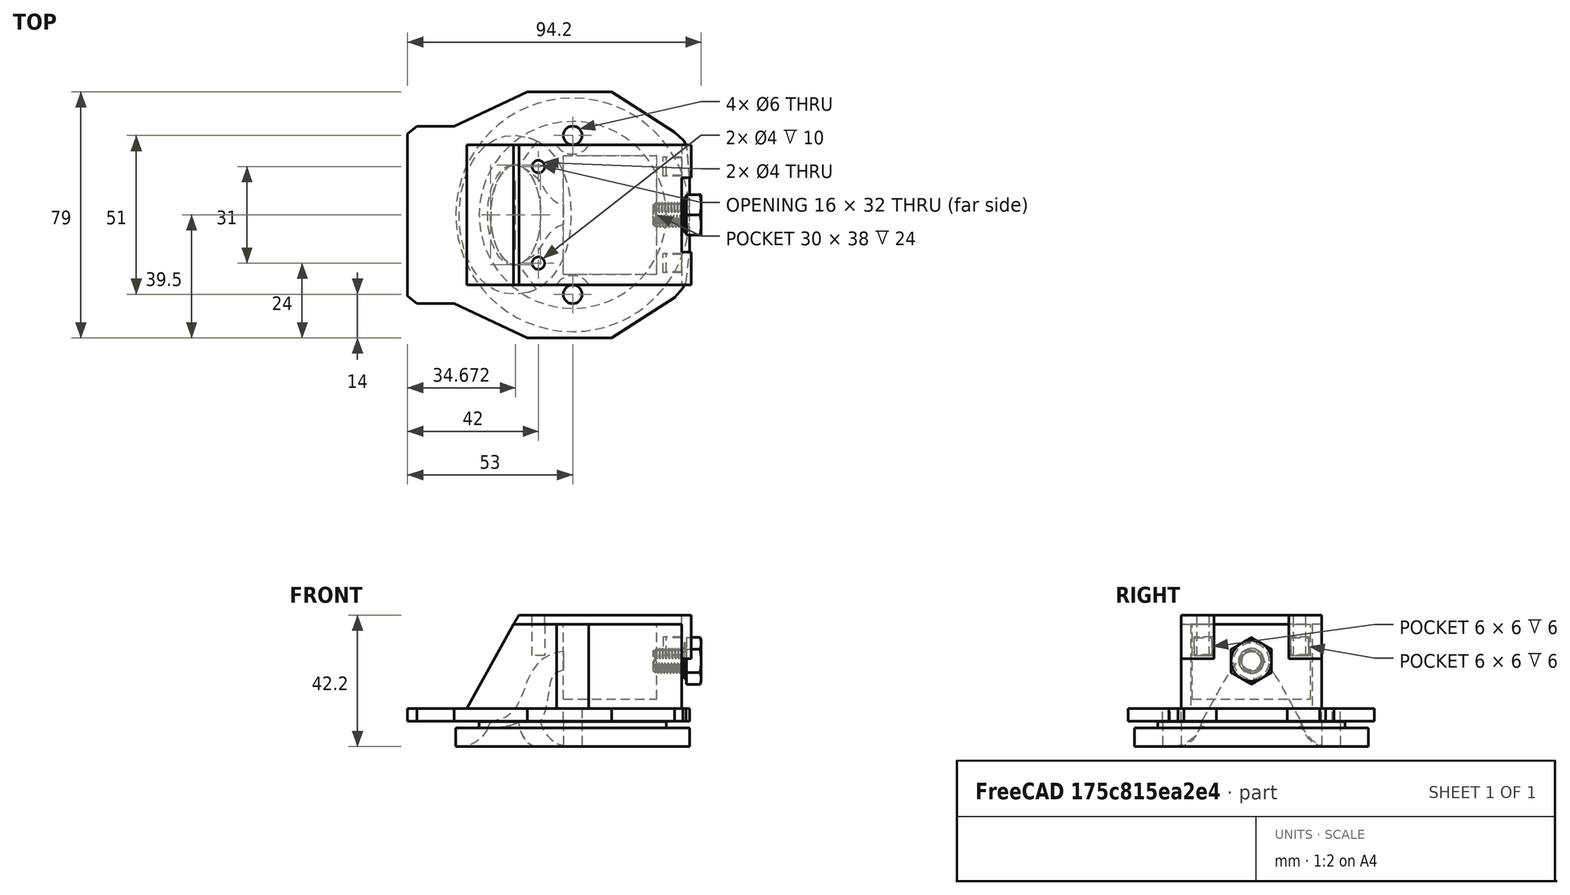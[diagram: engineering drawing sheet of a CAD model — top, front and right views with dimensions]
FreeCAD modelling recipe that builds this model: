
FCSTD DOCUMENT  (FreeCAD 1.0R39109 (Git))
Label: cup spool
License: All rights reserved
LicenseURL: https://en.wikipedia.org/wiki/All_rights_reserved
objects: Sketcher::SketchObject×17, PartDesign::Pad×6, Mesh::Feature×5, PartDesign::Pocket×4, PartDesign::Body×3, PartDesign::SubtractiveBox×1, Part::FeaturePython×1, PartDesign::SubtractivePipe×1, App::Part×1, PartDesign::AdditiveLoft×1, PartDesign::SubtractiveLoft×1, PartDesign::Fillet×1
note: 83 computed .brp shape members not serialized (recipe doc carries the construction recipe); baked Part::Feature solids carry a one-line shape summary decoded from their .brp

FEATURE [Mesh::Feature] cup_spool_bolt  label="bolt"
  Placement = pos=(23.83,0,17.89) rot=(0,1,0;0.785398rad)
FEATURE [Mesh::Feature] cup_spool_bottom_cylinder  label="cup spool bottom cylinder"
FEATURE [Mesh::Feature] cup_spool_cup_cylinder  label="cup spool cup cylinder"
FEATURE [Mesh::Feature] cup_spool_cup  label="cup spool cup"
  Placement = pos=(-0.2,1.9,-4) rot=(0,0,1;0rad)
FEATURE [Sketcher::SketchObject] Sketch
  ArcFitTolerance = 1e-06
  AttachmentSupport = -> [XY_Plane]
  FullyConstrained = true
  MakeInternals = false
  MapMode = 5
  sketch-geometry (1):
    g0: Circle CenterX=0 CenterY=0 CenterZ=0 NormalX=0 NormalY=0 NormalZ=1 AngleXU=0 Radius=37.5
  constraints (2):
    c: Coincident(g0,g-1)
    c: Diameter(g0) = 75
FEATURE [PartDesign::Pad] Pad
  Direction = (0,0,1)
  Length = 6
  Length2 = 10
  Profile = -> Sketch
  ReferenceAxis = -> Sketch [N_Axis]
  Refine = true
  Suppressed = false
  Type = 0
FEATURE [Sketcher::SketchObject] Sketch001
  ArcFitTolerance = 1e-06
  AttachmentSupport = -> [Pad]
  FullyConstrained = true
  MakeInternals = false
  MapMode = 5
  Placement = pos=(0,0,6) rot=(0,0,1;0rad)
  sketch-geometry (1):
    g0: Circle CenterX=0 CenterY=0 CenterZ=0 NormalX=0 NormalY=0 NormalZ=1 AngleXU=0 Radius=30
  constraints (2):
    c: Coincident(g0,g-1)
    c: Diameter(g0) = 60
FEATURE [PartDesign::Pad] Pad001
  BaseFeature = -> Pad
  Direction = (0,0,1)
  Length = 2
  Length2 = 10
  Profile = -> Sketch001
  ReferenceAxis = -> Sketch001 [N_Axis]
  Refine = true
  Suppressed = false
  Type = 0
FEATURE [Sketcher::SketchObject] Sketch002
  ArcFitTolerance = 1e-06
  AttachmentSupport = -> [XY_Plane001]
  FullyConstrained = true
  MakeInternals = false
  MapMode = 5
  sketch-geometry (18):
    g0: LineSegment StartX=-53 StartY=26 StartZ=0 EndX=-53 EndY=-26 EndZ=0
    g1: LineSegment StartX=-53 StartY=-26 StartZ=0 EndX=-50 EndY=-28.5 EndZ=0
    g2: LineSegment StartX=-50 StartY=-28.5 StartZ=0 EndX=-38 EndY=-28.5 EndZ=0
    g3: LineSegment StartX=-38 StartY=-28.5 StartZ=0 EndX=-14.5 EndY=-39.5 EndZ=0
    g4: LineSegment StartX=-14.5 StartY=-39.5 StartZ=0 EndX=12.5 EndY=-39.5 EndZ=0
    g5: LineSegment StartX=12.5 StartY=-39.5 StartZ=0 EndX=32.6742 EndY=-26.5 EndZ=0
    g6: LineSegment StartX=36.4381 StartY=-21.6053 StartZ=0 EndX=37.5 EndY=-11.2321 EndZ=0
    g7: LineSegment StartX=37.5 StartY=-11.2321 StartZ=0 EndX=37.5 EndY=11.5 EndZ=0
    g8: LineSegment StartX=37.5 StartY=11.5 StartZ=0 EndX=36.6742 EndY=21.8947 EndZ=0
    g9: LineSegment StartX=32.6742 StartY=26.5 StartZ=0 EndX=12.5 EndY=39.5 EndZ=0
    g10: LineSegment StartX=12.5 StartY=39.5 StartZ=0 EndX=-14.5 EndY=39.5 EndZ=0
    g11: LineSegment StartX=-14.5 StartY=39.5 StartZ=0 EndX=-38 EndY=28.5 EndZ=0
    g12: LineSegment StartX=-38 StartY=28.5 StartZ=0 EndX=-50 EndY=28.5 EndZ=0
    g13: LineSegment StartX=-50 StartY=28.5 StartZ=0 EndX=-53 EndY=26 EndZ=0
    g14: LineSegment StartX=32.6742 StartY=26.5 StartZ=0 EndX=35.6742 EndY=23.8542 EndZ=0
    g15: LineSegment StartX=35.6742 StartY=23.8542 StartZ=0 EndX=36.6742 EndY=21.8947 EndZ=0
    g16: LineSegment StartX=32.6742 StartY=-26.5 StartZ=0 EndX=35.32 EndY=-23.5 EndZ=0
    g17: LineSegment StartX=35.32 StartY=-23.5 StartZ=0 EndX=36.4381 EndY=-21.6053 EndZ=0
  constraints (54):
    c: Vertical(g0)
    c: Horizontal(g4)
    c: Vertical(g7)
    c: Horizontal(g10)
    c: DistanceY(g0,g0) = 52
    c: Distance(g0,g-1) = 26
    c: Distance(g-1,g0) = 53
    c: Coincident(g13,g0)
    c: Coincident(g1,g0)
    c: DistanceX(g0,g13) = 3
    c: DistanceY(g0,g13) = 2.5
    c: DistanceY(g1,g0) = 2.5
    c: DistanceX(g0,g1) = 3
    c: Parallel(g2,g-1)
    c: Parallel(g12,g-1)
    c: Coincident(g12,g13)
    c: DistanceX(g12,g12) = 12
    c: Coincident(g1,g2)
    c: Equal(g2,g12)
    c: Coincident(g2,g3)
    c: Coincident(g12,g11)
    c: Equal(g11,g3)
    c: Distance(g11,g-1) = 39.5
    c: Distance(g3,g-1) = 39.5
    c: DistanceX(g3,g-1) = 14.5
    c: Coincident(g10,g11)
    c: Coincident(g4,g3)
    c: Equal(g10,g4)
    c: DistanceX(g10,g10) = 27
    c: Coincident(g10,g9)
    c: Coincident(g4,g5)
    c: Equal(g5,g9)
    c: Distance(g5,g5) = 24
    c: DistanceY(g5,g-1) = 26.5
    c: Distance(g9,g-1) = 26.5
    c: Equal(g8,g6)
    c: Distance(g8,g-1) = 11.5
    c: Coincident(g6,g7)
    c: Coincident(g8,g7)
    c: Coincident(g5,g16)
    c: Coincident(g14,g9)
    c: Equal(g16,g14)
    c: DistanceX(g9,g14) = 3
    c: DistanceY(g5,g16) = 3
    c: Coincident(g16,g17)
    c: Coincident(g15,g14)
    c: Equal(g17,g15)
    c: Coincident(g17,g6)
    c: Coincident(g15,g8)
    c: Distance(g17,g17) = 2.2
    c: Distance(g16,g16) = 4
    c: DistanceY(g6,g8) = 43.5
    c: DistanceX(g14,g8) = 1
    c: Distance(g-2,g7) = 37.5
FEATURE [Mesh::Feature] cup_spool_cup001  label="cup spool cup001"
  Placement = pos=(-0.694658,0.312171,0) rot=(0,0,-1;0.017453rad)
FEATURE [PartDesign::Pad] Pad002
  Direction = (0,0,1)
  Length = 4
  Length2 = 10
  Profile = -> Sketch002
  ReferenceAxis = -> Sketch002 [N_Axis]
  Refine = true
  Suppressed = false
  Type = 0
FEATURE [Sketcher::SketchObject] Sketch003
  ArcFitTolerance = 1e-06
  AttachmentSupport = -> [XZ_Plane001]
  FullyConstrained = true
  MakeInternals = false
  MapMode = 5
  Placement = pos=(0,0,0) rot=(1,0,0;1.5708rad)
  sketch-geometry (4):
    g0: LineSegment StartX=35 StartY=31 StartZ=0 EndX=35 EndY=4 EndZ=0
    g1: LineSegment StartX=35 StartY=31 StartZ=0 EndX=-19 EndY=31 EndZ=0
    g2: LineSegment StartX=-19 StartY=31 StartZ=0 EndX=-34 EndY=4 EndZ=0
    g3: LineSegment StartX=35 StartY=4 StartZ=0 EndX=-34 EndY=4 EndZ=0
  constraints (12):
    c: Vertical(g0)
    c: Horizontal(g1)
    c: Horizontal(g3)
    c: DistanceY(g-1,g0) = 4
    c: Distance(g0,g-2) = 35
    c: DistanceY(g0,g0) = 27
    c: Coincident(g0,g3)
    c: DistanceX(g3,g3) = 69
    c: Coincident(g2,g3)
    c: Coincident(g1,g0)
    c: DistanceX(g1,g1) = 54
    c: Coincident(g2,g1)
FEATURE [PartDesign::Pad] Pad003
  BaseFeature = -> Pad002
  Direction = (0,-1,2e-16)
  Length = 45
  Length2 = 10
  Midplane = true
  Profile = -> Sketch003
  ReferenceAxis = -> Sketch003 [N_Axis]
  Refine = true
  Suppressed = false
  Type = 0
FEATURE [PartDesign::SubtractiveBox] Box
  AttacherType = Attacher::AttachEngine3D
  AttachmentOffset = pos=(-3,-19,7) rot=(0,0,1;0rad)
  AttachmentSupport = -> [XY_Plane001]
  BaseFeature = -> Pad003
  Height = 24
  Length = 30
  MapMode = 5
  Placement = pos=(-3,-19,7) rot=(0,0,1;0rad)
  Refine = true
  Suppressed = false
  Width = 38
FEATURE [Part::FeaturePython] Screw  label="M8x1x10-Screw"  # WARN: FeaturePython — macro-defined, semantics opaque (R4)
  Diameter = 1
  Invert = false
  LeftHanded = false
  Length = 8
  LengthCustom = 10
  MatchOuter = false
  OffsetAngle = 0
  Placement = pos=(35.9,0,19.3) rot=(0,1,0;1.5708rad)
  Thread = true
  Type = 91
FEATURE [Sketcher::SketchObject] Sketch004
  ArcFitTolerance = 1e-06
  AttachmentSupport = -> [Box]
  FullyConstrained = true
  MakeInternals = false
  MapMode = 5
  Placement = pos=(35,-19,7) rot=(0.57735,0.57735,0.57735;2.0944rad)
  sketch-geometry (8):
    g0: LineSegment StartX=0.5 StartY=20 StartZ=0 EndX=0.5 EndY=14 EndZ=0
    g1: LineSegment StartX=0.5 StartY=14 StartZ=0 EndX=6.5 EndY=14 EndZ=0
    g2: LineSegment StartX=6.5 StartY=14 StartZ=0 EndX=6.5 EndY=20 EndZ=0
    g3: LineSegment StartX=6.5 StartY=20 StartZ=0 EndX=0.5 EndY=20 EndZ=0
    g4: LineSegment StartX=31.5 StartY=20 StartZ=0 EndX=31.5 EndY=14 EndZ=0
    g5: LineSegment StartX=31.5 StartY=14 StartZ=0 EndX=37.5 EndY=14 EndZ=0
    g6: LineSegment StartX=37.5 StartY=14 StartZ=0 EndX=37.5 EndY=20 EndZ=0
    g7: LineSegment StartX=37.5 StartY=20 StartZ=0 EndX=31.5 EndY=20 EndZ=0
  constraints (24):
    c: Coincident(g0,g1)
    c: Coincident(g1,g2)
    c: Coincident(g2,g3)
    c: Coincident(g3,g0)
    c: Vertical(g0)
    c: Vertical(g2)
    c: Horizontal(g1)
    c: Horizontal(g3)
    c: Coincident(g4,g5)
    c: Coincident(g5,g6)
    c: Coincident(g6,g7)
    c: Coincident(g7,g4)
    c: Vertical(g4)
    c: Vertical(g6)
    c: Horizontal(g5)
    c: Horizontal(g7)
    c: DistanceX(g3,g3) = 6
    c: Equal(g3,g7)
    c: Equal(g2,g3)
    c: Equal(g4,g7)
    c: Distance(g-2,g0) = 0.5
    c: Distance(g-2,g6) = 37.5
    c: Distance(g-1,g1) = 14
    c: Distance(g-1,g5) = 14
FEATURE [PartDesign::Pocket] Pocket
  BaseFeature = -> Box
  Direction = (-1,0,0)
  Length = 6
  Length2 = 5
  Placement = pos=(-3,-19,7) rot=(0,0,1;0rad)
  Profile = -> Sketch004
  ReferenceAxis = -> Sketch004 [N_Axis]
  Refine = true
  Suppressed = false
  Type = 0
FEATURE [Sketcher::SketchObject] Sketch005
  ArcFitTolerance = 1e-06
  AttachmentSupport = -> [Pocket]
  FullyConstrained = true
  MakeInternals = false
  MapMode = 5
  Placement = pos=(-3,-19,31) rot=(0,0,1;0rad)
  sketch-geometry (2):
    g0: Circle CenterX=-8 CenterY=34.5 CenterZ=0 NormalX=0 NormalY=0 NormalZ=1 AngleXU=0 Radius=2
    g1: Circle CenterX=-8 CenterY=3.5 CenterZ=0 NormalX=0 NormalY=0 NormalZ=1 AngleXU=0 Radius=2
  constraints (6):
    c: Diameter(g0) = 4
    c: Diameter(g1) = 4
    c: Distance(g0,g-1) = 34.5
    c: Distance(g1,g-1) = 3.5
    c: Distance(g1,g-2) = 8
    c: Distance(g0,g-2) = 8
FEATURE [PartDesign::Pocket] Pocket001
  BaseFeature = -> Pocket
  Direction = (0,0,-1)
  Length = 10
  Length2 = 5
  Placement = pos=(-3,-19,7) rot=(0,0,1;0rad)
  Profile = -> Sketch005
  ReferenceAxis = -> Sketch005 [N_Axis]
  Refine = true
  Suppressed = false
  Type = 0
FEATURE [Sketcher::SketchObject] Sketch007  label="hole cleaner box"
  ArcFitTolerance = 1e-06
  AttachmentSupport = -> [Pocket001]
  FullyConstrained = false
  MakeInternals = false
  MapMode = 5
  Placement = pos=(-3,-19,7) rot=(0.57735,0.57735,0.57735;2.0944rad)
  sketch-geometry (1):
    g0: Circle CenterX=18.991 CenterY=12.3351 CenterZ=0 NormalX=0 NormalY=0 NormalZ=1 AngleXU=0 Radius=3
  constraints (1):
    c: Diameter(g0) = 6
FEATURE [Sketcher::SketchObject] Sketch008  label="hole bottom"
  ArcFitTolerance = 1e-06
  AttachmentSupport = -> [Pocket001]
  FullyConstrained = false
  MakeInternals = false
  MapMode = 5
  Placement = pos=(-3,-19,0) rot=(1,0,0;3.14159rad)
  sketch-geometry (5):
    g0: Ellipse CenterX=-15.3285 CenterY=-19 CenterZ=0 NormalX=0 NormalY=0 NormalZ=1 MajorRadius=16 MinorRadius=8 AngleXU=-1.5708
    g1: LineSegment [constr] StartX=-15.3285 StartY=-35 StartZ=0 EndX=-15.3285 EndY=-3 EndZ=0
    g2: LineSegment [constr] StartX=-7.32854 StartY=-19 StartZ=0 EndX=-23.3285 EndY=-19 EndZ=0
    g3: GeomPoint [constr] X=-15.3285 Y=-32.8564 Z=0
    g4: GeomPoint [constr] X=-15.3285 Y=-5.14359 Z=0
  constraints (5):
    c: InternalAlignment(g1-g4 -> g0) x4
    c: Distance(g0,g1) = 16
    c: Angle(g1) = 1.5708
    c: Distance(g0,g2) = 8
    c: Distance(g0,g-1) = 19
FEATURE [Sketcher::SketchObject] Sketch009  label="hole path"
  ArcFitTolerance = 1e-06
  AttachmentSupport = -> [XZ_Plane001]
  FullyConstrained = false
  MakeInternals = false
  MapMode = 5
  Placement = pos=(0,0,0) rot=(1,0,0;1.5708rad)
  sketch-geometry (7):
    g0-g3: Circle [constr] x4 (B-spline internal-alignment scaffolding for g4; pole/knot coordinates omitted)
    g4: BSplineCurve PolesCount=4 KnotsCount=2 Degree=3 IsPeriodic=0
    g5: GeomPoint [constr] X=-19.2845 Y=0 Z=0
    g6: GeomPoint [constr] X=-3.01587 Y=19.3204 Z=0
  constraints (8):
    c: Weight(g0) = 1
    c: Equal(g0,g1)
    c: Equal(g0,g2)
    c: Equal(g0,g3)
    c: InternalAlignment(g0-g3 -> g4) x4
    c: InternalAlignment(g5,g4)
    c: InternalAlignment(g6,g4)
    c: PointOnObject(g0,g-1)
FEATURE [PartDesign::SubtractivePipe] SubtractivePipe
  AuxilleryCurvelinear = true
  AuxillerySpineTangent = false
  BaseFeature = -> Pocket001
  Binormal = (0,0,0)
  Mode = 0
  Placement = pos=(-3,-19,7) rot=(0,0,1;0rad)
  Profile = -> Sketch007
  Refine = true
  Sections = -> [Sketch008]
  Spine = -> Sketch009
  SpineTangent = false
  Suppressed = false
  Transformation = 1
  Transition = 0
FEATURE [App::Part] Part  label="import"
  Group = -> [cup_spool_bottom_cylinder,cup_spool_cup_cylinder,cup_spool_cup,cup_spool_cup001]
  Origin = -> Origin003
FEATURE [Sketcher::SketchObject] Sketch010
  ArcFitTolerance = 1e-06
  AttachmentSupport = -> [XY_Plane002]
  FullyConstrained = true
  MakeInternals = false
  MapMode = 5
  sketch-geometry (6):
    g0: LineSegment StartX=-31 StartY=22.5 StartZ=0 EndX=-31 EndY=-22.5 EndZ=0
    g1: LineSegment StartX=-31 StartY=-22.5 StartZ=0 EndX=23 EndY=-22.5 EndZ=0
    g2: LineSegment StartX=23 StartY=-22.5 StartZ=0 EndX=23 EndY=22.5 EndZ=0
    g3: LineSegment StartX=23 StartY=22.5 StartZ=0 EndX=-31 EndY=22.5 EndZ=0
    g4: Circle CenterX=-23 CenterY=15.5 CenterZ=0 NormalX=0 NormalY=0 NormalZ=1 AngleXU=0 Radius=2
    g5: Circle CenterX=-23 CenterY=-15.5 CenterZ=0 NormalX=0 NormalY=0 NormalZ=1 AngleXU=0 Radius=2
  constraints (18):
    c: Coincident(g0,g1)
    c: Coincident(g1,g2)
    c: Coincident(g2,g3)
    c: Coincident(g3,g0)
    c: Vertical(g0)
    c: Vertical(g2)
    c: Horizontal(g1)
    c: Horizontal(g3)
    c: Distance(g-1,g1) = 22.5
    c: DistanceY(g0,g0) = 45
    c: DistanceX(g1,g1) = 54
    c: Diameter(g4) = 4
    c: Diameter(g5) = 4
    c: Distance(g5,g-2) = 23
    c: DistanceY(g5,g-1) = 15.5
    c: DistanceY(g-1,g4) = 15.5
    c: DistanceX(g4,g-1) = 23
    c: Distance(g2,g-2) = 23
FEATURE [Sketcher::SketchObject] Sketch011
  ArcFitTolerance = 1e-06
  AttachmentOffset = pos=(0,0,3) rot=(0,0,1;0rad)
  AttachmentSupport = -> [XY_Plane002]
  FullyConstrained = true
  MakeInternals = false
  MapMode = 5
  Placement = pos=(0,0,3) rot=(0,0,1;0rad)
  sketch-geometry (6):
    g0: LineSegment StartX=-29.25 StartY=22.5 StartZ=0 EndX=-29.25 EndY=-22.5 EndZ=0
    g1: LineSegment StartX=-29.25 StartY=-22.5 StartZ=0 EndX=23 EndY=-22.5 EndZ=0
    g2: LineSegment StartX=23 StartY=-22.5 StartZ=0 EndX=23 EndY=22.5 EndZ=0
    g3: LineSegment StartX=23 StartY=22.5 StartZ=0 EndX=-29.25 EndY=22.5 EndZ=0
    g4: Circle CenterX=-23 CenterY=15.5 CenterZ=0 NormalX=0 NormalY=0 NormalZ=1 AngleXU=0 Radius=2
    g5: Circle CenterX=-23 CenterY=-15.5 CenterZ=0 NormalX=0 NormalY=0 NormalZ=1 AngleXU=0 Radius=2
  constraints (18):
    c: Coincident(g0,g1)
    c: Coincident(g1,g2)
    c: Coincident(g2,g3)
    c: Coincident(g3,g0)
    c: Vertical(g0)
    c: Vertical(g2)
    c: Horizontal(g1)
    c: Horizontal(g3)
    c: Distance(g-2,g2) = 23
    c: Distance(g-1,g3) = 22.5
    c: Distance(g1,g-1) = 22.5
    c: Distance(g0,g-2) = 29.25
    c: Diameter(g4) = 4
    c: Diameter(g5) = 4
    c: Distance(g5,g-1) = 15.5
    c: Distance(g4,g-1) = 15.5
    c: Distance(g4,g-2) = 23
    c: Distance(g5,g-2) = 23
FEATURE [PartDesign::AdditiveLoft] AdditiveLoft
  Closed = false
  Profile = -> Sketch010
  Refine = true
  Ruled = false
  Sections = -> [Sketch011]
  Suppressed = false
FEATURE [Sketcher::SketchObject] Sketch012
  ArcFitTolerance = 1e-06
  AttachmentSupport = -> [AdditiveLoft]
  FullyConstrained = true
  MakeInternals = false
  MapMode = 5
  Placement = pos=(23,0,0) rot=(0.57735,0.57735,0.57735;2.0944rad)
  sketch-geometry (8):
    g0: LineSegment StartX=-22.5 StartY=3 StartZ=0 EndX=-22.5 EndY=-11 EndZ=0
    g1: LineSegment StartX=-22.5 StartY=-11 StartZ=0 EndX=-12 EndY=-11 EndZ=0
    g2: LineSegment StartX=-12 StartY=-11 StartZ=0 EndX=-12 EndY=3 EndZ=0
    g3: LineSegment StartX=-12 StartY=3 StartZ=0 EndX=-22.5 EndY=3 EndZ=0
    g4: LineSegment StartX=12 StartY=3 StartZ=0 EndX=12 EndY=-11 EndZ=0
    g5: LineSegment StartX=12 StartY=-11 StartZ=0 EndX=22.5 EndY=-11 EndZ=0
    g6: LineSegment StartX=22.5 StartY=-11 StartZ=0 EndX=22.5 EndY=3 EndZ=0
    g7: LineSegment StartX=22.5 StartY=3 StartZ=0 EndX=12 EndY=3 EndZ=0
  constraints (24):
    c: Coincident(g0,g1)
    c: Coincident(g1,g2)
    c: Coincident(g2,g3)
    c: Coincident(g3,g0)
    c: Vertical(g0)
    c: Vertical(g2)
    c: Horizontal(g1)
    c: Horizontal(g3)
    c: Distance(g0,g2) = 10.5
    c: Distance(g1,g3) = 14
    c: Distance(g-2,g2) = 12
    c: Distance(g2,g-1) = 3
    c: Coincident(g4,g5)
    c: Coincident(g5,g6)
    c: Coincident(g6,g7)
    c: Coincident(g7,g4)
    c: Vertical(g4)
    c: Vertical(g6)
    c: Horizontal(g5)
    c: Horizontal(g7)
    c: Distance(g4,g6) = 10.5
    c: Distance(g5,g7) = 14
    c: Distance(g-1,g7) = 3
    c: Distance(g4,g-2) = 12
FEATURE [PartDesign::Pad] Pad004
  BaseFeature = -> AdditiveLoft
  Direction = (1,0,0)
  Length = 3
  Length2 = 10
  Profile = -> Sketch012
  ReferenceAxis = -> Sketch012 [N_Axis]
  Refine = true
  Suppressed = false
  Type = 0
FEATURE [Sketcher::SketchObject] Sketch013
  ArcFitTolerance = 1e-06
  AttachmentSupport = -> [Pad004]
  FullyConstrained = true
  MakeInternals = false
  MapMode = 5
  Placement = pos=(23,0,0) rot=(0.57735,-0.57735,-0.57735;2.0944rad)
  sketch-geometry (8):
    g0: LineSegment StartX=12.75 StartY=-4.25 StartZ=0 EndX=12.75 EndY=-9.75 EndZ=0
    g1: LineSegment StartX=12.75 StartY=-9.75 StartZ=0 EndX=18.25 EndY=-9.75 EndZ=0
    g2: LineSegment StartX=18.25 StartY=-9.75 StartZ=0 EndX=18.25 EndY=-4.25 EndZ=0
    g3: LineSegment StartX=18.25 StartY=-4.25 StartZ=0 EndX=12.75 EndY=-4.25 EndZ=0
    g4: LineSegment StartX=-18.25 StartY=-4.25 StartZ=0 EndX=-18.25 EndY=-9.75 EndZ=0
    g5: LineSegment StartX=-18.25 StartY=-9.75 StartZ=0 EndX=-12.75 EndY=-9.75 EndZ=0
    g6: LineSegment StartX=-12.75 StartY=-9.75 StartZ=0 EndX=-12.75 EndY=-4.25 EndZ=0
    g7: LineSegment StartX=-12.75 StartY=-4.25 StartZ=0 EndX=-18.25 EndY=-4.25 EndZ=0
  constraints (24):
    c: Coincident(g0,g1)
    c: Coincident(g1,g2)
    c: Coincident(g2,g3)
    c: Coincident(g3,g0)
    c: Vertical(g0)
    c: Vertical(g2)
    c: Horizontal(g1)
    c: Horizontal(g3)
    c: Coincident(g4,g5)
    c: Coincident(g5,g6)
    c: Coincident(g6,g7)
    c: Coincident(g7,g4)
    c: Vertical(g4)
    c: Vertical(g6)
    c: Horizontal(g5)
    c: Horizontal(g7)
    c: Equal(g5,g1)
    c: Equal(g0,g6)
    c: DistanceX(g1,g1) = 5.5
    c: DistanceX(g-1,g0) = 12.75
    c: DistanceY(g2,g2) = 5.5
    c: DistanceY(g2,g-1) = 4.25
    c: Distance(g6,g-2) = 12.75
    c: Distance(g6,g-1) = 4.25
FEATURE [PartDesign::Pad] Pad005
  BaseFeature = -> Pad004
  Direction = (-1,0,0)
  Length = 5
  Length2 = 10
  Profile = -> Sketch013
  ReferenceAxis = -> Sketch013 [N_Axis]
  Refine = true
  Suppressed = false
  Type = 0
FEATURE [PartDesign::Body] Body002  label="top lid cover"
  AllowCompound = false
  Group = -> [Sketch010,Sketch011,AdditiveLoft,Sketch012,Pad004,Sketch013,Pad005]
  Origin = -> Origin002
  Placement = pos=(12,0,31) rot=(0,0,1;0rad)
  Tip = -> Pad005
FEATURE [Sketcher::SketchObject] Sketch014
  ArcFitTolerance = 1e-06
  AttachmentSupport = -> [Pad001]
  FullyConstrained = true
  MakeInternals = false
  MapMode = 5
  Placement = pos=(0,0,8) rot=(0,0,1;0rad)
  sketch-geometry (7):
    g0: Ellipse CenterX=-18.3 CenterY=0 CenterZ=0 NormalX=0 NormalY=0 NormalZ=1 MajorRadius=16 MinorRadius=8 AngleXU=-1.5708
    g1: LineSegment [constr] StartX=-18.3 StartY=-16 StartZ=0 EndX=-18.3 EndY=16 EndZ=0
    g2: LineSegment [constr] StartX=-10.3 StartY=-2.61436e-06 StartZ=0 EndX=-26.3 EndY=2.61436e-06 EndZ=0
    g3: GeomPoint [constr] X=-18.3 Y=-13.8564 Z=0
    g4: GeomPoint [constr] X=-18.3 Y=13.8564 Z=0
    g5: Circle CenterX=0 CenterY=25.5 CenterZ=0 NormalX=0 NormalY=0 NormalZ=1 AngleXU=0 Radius=3
    g6: Circle CenterX=0 CenterY=-25.5 CenterZ=0 NormalX=0 NormalY=0 NormalZ=1 AngleXU=0 Radius=3
  constraints (12):
    c: InternalAlignment(g1-g4 -> g0) x4
    c: Distance(g0,g1) = 16
    c: Angle(g1) = 1.5708
    c: Distance(g0,g2) = 8
    c: PointOnObject(g0,g-1)
    c: DistanceX(g0,g-1) = 18.3
    c: Diameter(g5) = 6
    c: PointOnObject(g5,g-2)
    c: Diameter(g6) = 6
    c: PointOnObject(g6,g-2)
    c: Distance(g6,g-1) = 25.5
    c: DistanceY(g-1,g5) = 25.5
FEATURE [Sketcher::SketchObject] Sketch015
  ArcFitTolerance = 1e-06
  AttachmentSupport = -> [Pad001]
  FullyConstrained = true
  MakeInternals = false
  MapMode = 5
  Placement = pos=(0,0,0) rot=(1,0,0;3.14159rad)
  sketch-geometry (7):
    g0: Ellipse CenterX=-20.2 CenterY=0 CenterZ=0 NormalX=0 NormalY=0 NormalZ=1 MajorRadius=18 MinorRadius=9.8 AngleXU=-1.5708
    g1: LineSegment [constr] StartX=-20.2 StartY=-18 StartZ=0 EndX=-20.2 EndY=18 EndZ=0
    g2: LineSegment [constr] StartX=-10.4 StartY=-3.20259e-06 StartZ=0 EndX=-30 EndY=3.20259e-06 EndZ=0
    g3: GeomPoint [constr] X=-20.2 Y=-15.0983 Z=0
    g4: GeomPoint [constr] X=-20.2 Y=15.0983 Z=0
    g5: Circle CenterX=0 CenterY=-25.5 CenterZ=0 NormalX=0 NormalY=0 NormalZ=1 AngleXU=0 Radius=3
    g6: Circle CenterX=0 CenterY=25.5 CenterZ=0 NormalX=0 NormalY=0 NormalZ=1 AngleXU=0 Radius=3
  constraints (12):
    c: InternalAlignment(g1-g4 -> g0) x4
    c: Distance(g0,g1) = 18
    c: Angle(g1) = 1.5708
    c: Distance(g0,g2) = 9.8
    c: PointOnObject(g0,g-1)
    c: Distance(g1,g-2) = 20.2
    c: Diameter(g5) = 6
    c: PointOnObject(g5,g-2)
    c: Diameter(g6) = 6
    c: PointOnObject(g6,g-2)
    c: Distance(g6,g-1) = 25.5
    c: DistanceY(g5,g-1) = 25.5
FEATURE [PartDesign::SubtractiveLoft] SubtractiveLoft
  BaseFeature = -> Pad001
  Closed = false
  Profile = -> Sketch014
  Refine = true
  Ruled = false
  Sections = -> [Sketch015]
  Suppressed = false
FEATURE [PartDesign::Fillet] Fillet
  Base = -> SubtractiveLoft [Edge5]
  BaseFeature = -> SubtractiveLoft
  Radius = 10
  Refine = true
  SupportTransform = false
  Suppressed = false
  UseAllEdges = false
FEATURE [PartDesign::Body] Body  label="bottom"
  AllowCompound = false
  Group = -> [Sketch,Pad,Sketch001,Pad001,Sketch014,Sketch015,SubtractiveLoft,Fillet]
  Origin = -> Origin
  Placement = pos=(0,0,-8.2) rot=(0,0,1;0rad)
  Tip = -> Fillet
FEATURE [Sketcher::SketchObject] Sketch016
  ArcFitTolerance = 1e-06
  AttachmentSupport = -> [SubtractivePipe]
  FullyConstrained = true
  MakeInternals = false
  MapMode = 5
  Placement = pos=(-3,-19,4) rot=(0,0,1;0rad)
  sketch-geometry (2):
    g0: Circle CenterX=3 CenterY=-6.5 CenterZ=0 NormalX=0 NormalY=0 NormalZ=1 AngleXU=0 Radius=6
    g1: Circle CenterX=3 CenterY=44.5 CenterZ=0 NormalX=0 NormalY=0 NormalZ=1 AngleXU=0 Radius=6
  constraints (6):
    c: Diameter(g0) = 12
    c: Diameter(g1) = 12
    c: Distance(g0,g-2) = 3
    c: Distance(g0,g-1) = 6.5
    c: Distance(g1,g-2) = 3
    c: DistanceY(g-1,g1) = 44.5
FEATURE [PartDesign::Pocket] Pocket002
  BaseFeature = -> SubtractivePipe
  Direction = (0,0,-1)
  Length = 27
  Length2 = 5
  Placement = pos=(-3,-19,7) rot=(0,0,1;0rad)
  Profile = -> Sketch016
  ReferenceAxis = -> Sketch016 [N_Axis]
  Refine = true
  Reversed = true
  Suppressed = false
  Type = 0
FEATURE [Sketcher::SketchObject] Sketch017
  ArcFitTolerance = 1e-06
  AttachmentSupport = -> [Pocket002]
  FullyConstrained = true
  MakeInternals = false
  MapMode = 5
  Placement = pos=(-3,-19,4) rot=(0,0,1;0rad)
  sketch-geometry (2):
    g0: Circle CenterX=3 CenterY=-6.5 CenterZ=0 NormalX=0 NormalY=0 NormalZ=1 AngleXU=0 Radius=3
    g1: Circle CenterX=3 CenterY=44.5 CenterZ=0 NormalX=0 NormalY=0 NormalZ=1 AngleXU=0 Radius=3
  constraints (6):
    c: Diameter(g0) = 6
    c: Diameter(g1) = 6
    c: DistanceX(g-1,g0) = 3
    c: Distance(g0,g-1) = 6.5
    c: Distance(g1,g-2) = 3
    c: DistanceY(g-1,g1) = 44.5
FEATURE [PartDesign::Pocket] Pocket003
  BaseFeature = -> Pocket002
  Direction = (0,0,-1)
  Length = 4
  Length2 = 5
  Placement = pos=(-3,-19,7) rot=(0,0,1;0rad)
  Profile = -> Sketch017
  ReferenceAxis = -> Sketch017 [N_Axis]
  Refine = true
  Suppressed = false
  Type = 0
FEATURE [PartDesign::Body] Body001  label="top lid"
  AllowCompound = false
  Group = -> [Sketch002,Pad002,Sketch003,Pad003,Box,Sketch004,Pocket,Sketch005,Pocket001,Sketch007,Sketch008,Sketch009,SubtractivePipe,Sketch016,Pocket002,Sketch017,Pocket003]
  Origin = -> Origin001
  Tip = -> Pocket003
